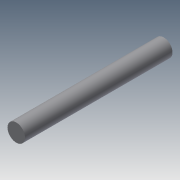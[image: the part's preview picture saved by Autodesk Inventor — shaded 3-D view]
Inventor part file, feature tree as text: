
AUTODESK INVENTOR PART (.ipt)
format: ipt  version: 2013 (Build 170138000, 138)  size: 66,048 bytes
history: native  units: mm
features: extrude x1, sketch x1
ambient origin geometry x8: Origin, YZ Plane, XZ Plane, XY Plane, X Axis, Y Axis, Z Axis, Center Point
bodies: Solid1 (feature_tree)
feature tree (2):
  extrude  "Extrusion1"  Depth=50.4mm TaperAngle=0.0deg
  sketch  "Sketch1"  dims[d0=6.0mm d1=50.4mm d2=0.0mm]
